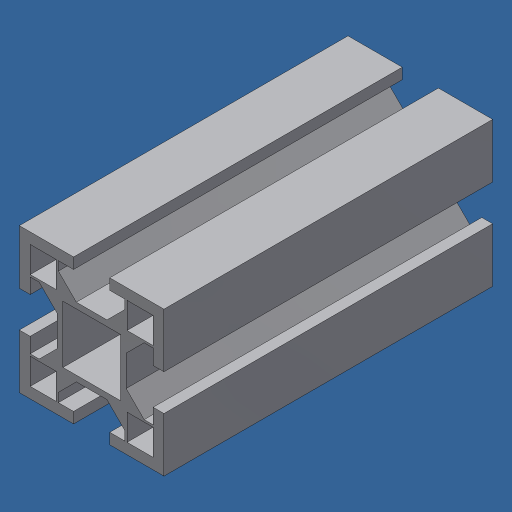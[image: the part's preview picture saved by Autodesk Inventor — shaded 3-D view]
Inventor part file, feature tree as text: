
AUTODESK INVENTOR PART (.ipt)
format: ipt  version: 2024.3 (Build 283343000, 343)  size: 221,184 bytes
history: native  units: mm (DEFAULTED — no unit token found)
features: extrude x4, other x2, sketch x1
ambient origin geometry x8: Origin, YZ Plane, XZ Plane, XY Plane, X Axis, Y Axis, Z Axis, Center Point
bodies: Body1 (feature_tree)
feature tree (7):
  other  "Finish - None"
  extrude  "JOKAB, 44MM"  Depth=44.0mm
  other  "Work Axis4"
  extrude  "Extrusion2"  Depth=100.0mm TaperAngle=0.0deg
  extrude  "Extrusion3"  Depth=17.4625mm
  extrude  "Extrusion4"  Depth=17.4625mm
  sketch  "Sketch2"  dims[d5=44.0mm d6=44.0mm d7=100.0mm d8=0.0mm d10=5.5mm d11=10.125mm d12=11.5mm d13=45.0deg d14=8.0mm d15=2.733333mm d17=8.2mm d18=40.0mm d20=360.0deg d22=10.0mm d23=0.0mm d28=10.0mm d29=0.0mm d30=3.3mm d31=3.3mm d32=7.9375mm d33=7.9375mm d34=10.0mm d35=0.0mm d36=17.4625mm d37=8.73125mm d38=17.4625mm d39=8.73125mm]
